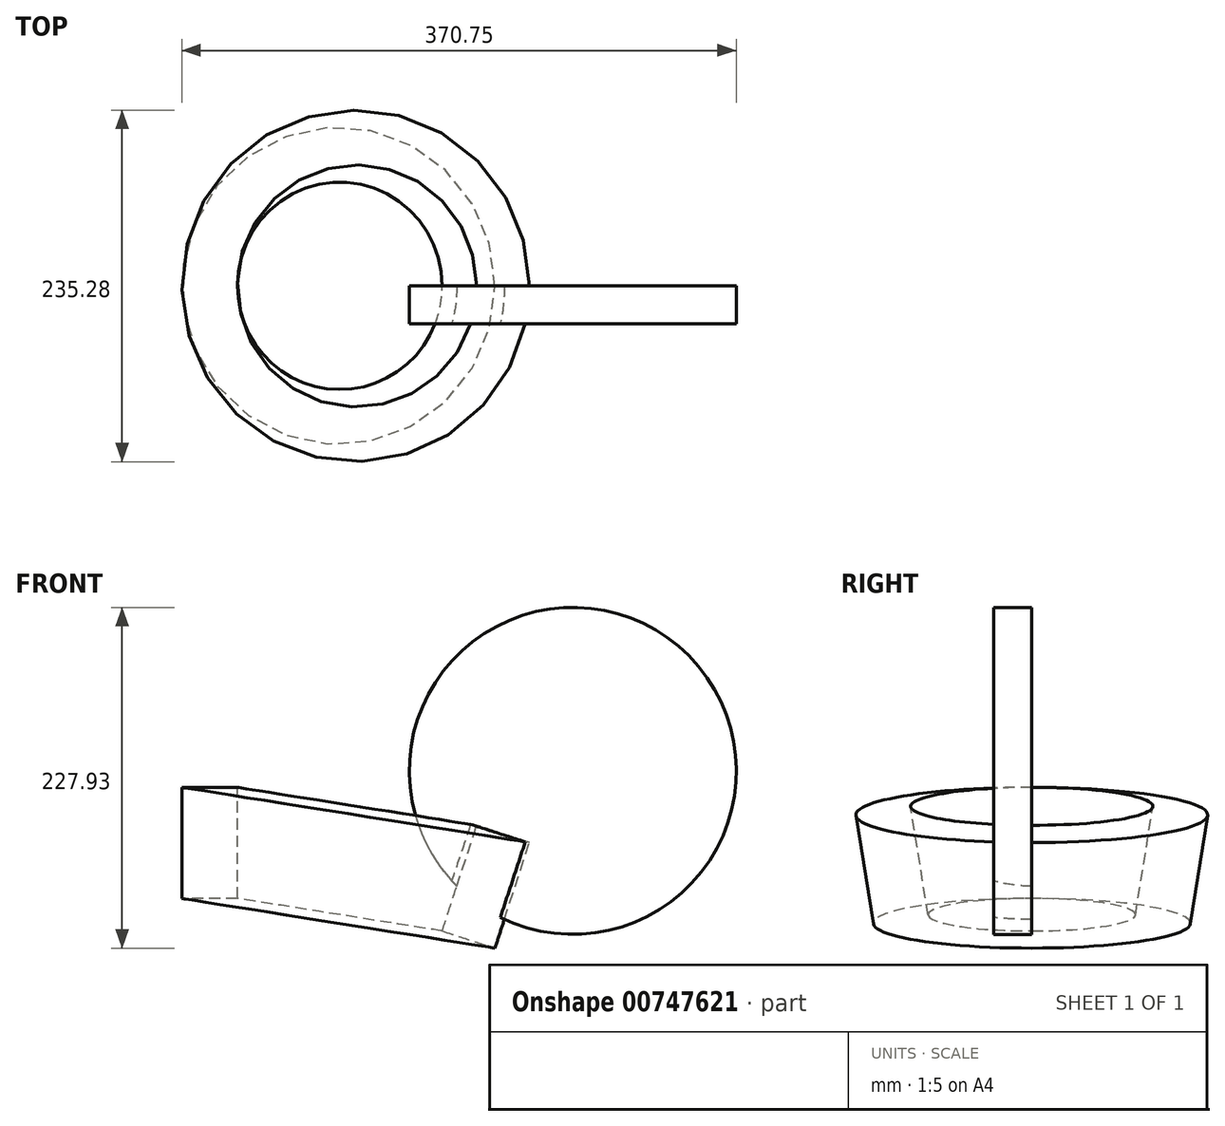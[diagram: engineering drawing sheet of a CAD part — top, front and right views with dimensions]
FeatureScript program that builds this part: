
annotation { "Feature Type Name" : "Feature", "Feature Type Description" : "" }
export const myFeature = defineFeature(function(context is Context, id is Id, definition is map)
    precondition{}
    {
        {
            var Q0;
            Q0=qCreatedBy(makeId("Front.planeOp"),FACE);
            var sketch = newSketch(context, id + "F0", { "sketchPlane" : qUnion([Q0])});
            skLineSegment(sketch, "E0", {"start": v(-92.45, 146.34) * mm, "end": v(-135.8, -126.5) * mm});
            skSolve(sketch);
        }
        {
            var Q0;
            Q0=qCreatedBy(makeId("Front.planeOp"),FACE);
            var sketch = newSketch(context, id + "F1", { "sketchPlane" : qUnion([Q0])});
            skLineSegment(sketch, "E1.bottom", {"start": v(-221.96, 80.93) * mm, "end": v(-184.85, 80.93) * mm});
            skLineSegment(sketch, "E1.top", {"start": v(-221.96, 6.62) * mm, "end": v(-184.85, 6.62) * mm});
            skLineSegment(sketch, "E1.left", {"start": v(-221.96, 80.93) * mm, "end": v(-221.96, 6.62) * mm});
            skLineSegment(sketch, "E1.right", {"start": v(-184.85, 80.93) * mm, "end": v(-184.85, 6.62) * mm});
            skSolve(sketch);
        }
        {
            var Q0;
            Q0=makeQuery(id+"F1.imprint","IMPRINT",FACE,{"disambiguationData":[TD([[makeQuery(id+"F1.imprint","IMPRINT",EDGE,{"derivedFrom":sQuery(id+"F1.wireOp",EDGE,"E1.bottom")}),-1.0]])]});
            var Q1;
            Q1=sQuery(id+"F0.wireOp",EDGE,"E0");
            revolve(context, id + "F2", {"surfaceOperationType" : NewSurfaceOperationType.NEW, "entities" : qUnion([Q0]), "axis" : qUnion([Q1]), "revolveType" : RevolveType.FULL});
        }
        {
            var Q0;
            Q0=qCreatedBy(makeId("Front.planeOp"),FACE);
            var sketch = newSketch(context, id + "F3", { "sketchPlane" : qUnion([Q0])});
            skCircle(sketch, "E2", {"center": v(39.42, 91.92) * mm, "radius": 109.37 * mm});
            skSolve(sketch);
        }
        {
            var Q0;
            Q0 = qSketchRegion(id + "F3", true);
            extrude(context, id + "F4", {"entities" : qUnion([Q0]), "operationType" : NewBodyOperationType.ADD, "depth" : 25.4 * mm, "offsetDistance" : 25.4 * mm});
        }
    });
